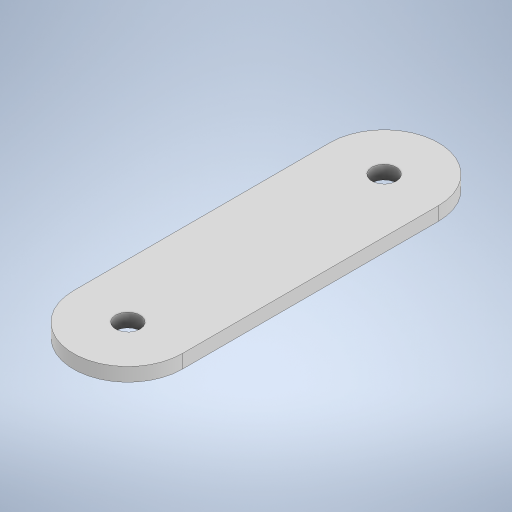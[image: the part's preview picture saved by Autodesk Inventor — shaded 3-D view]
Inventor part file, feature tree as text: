
AUTODESK INVENTOR PART (.ipt)
format: ipt  version: 2024.1 (Build 281209000, 209)  size: 226,304 bytes
history: native  units: mm
features: other x1, extrude x1, sketch x1
ambient origin geometry x8: Origin, YZ Plane, XZ Plane, XY Plane, X Axis, Y Axis, Z Axis, Center Point
bodies: Body1 (feature_tree)
feature tree (3):
  other  "ソリッド1"
  extrude  "押し出し1"  Depth=47.1mm
  sketch  "スケッチ1"
